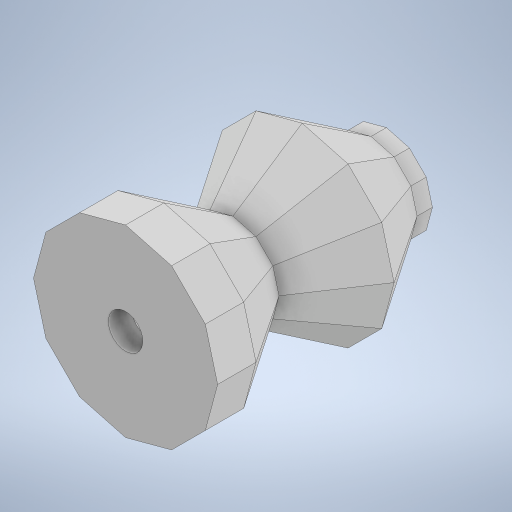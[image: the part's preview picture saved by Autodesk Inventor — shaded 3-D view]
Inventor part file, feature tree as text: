
AUTODESK INVENTOR PART (.ipt)
format: ipt  version: 2023 (Build 270158000, 158)  size: 360,448 bytes
history: native  units: in
note: dims shown in document units (in); Inventor stores cm internally (conversion verified against a paired STEP export)
features: sketch x6, extrude x4, projected_geometry x3, other x2, mirror x2, loft x1, shell x1
ambient origin geometry x8: Origin, YZ Plane, XZ Plane, XY Plane, X Axis, Y Axis, Z Axis, Center Point
bodies: Body1 (feature_tree)
feature tree (19):
  other  "솔리드1"
  sketch  "스케치1"
  other  "작업 평면1"
  loft  "로프트1"
  mirror  "미러1"
  mirror  "미러2"
  extrude  "돌출1"  Depth=0.3543in
  shell  "쉘4"  Thickness=0.4724in
  extrude  "돌출11"  TaperAngle=0.0deg  [1 undecoded]
  extrude  "돌출12"  TaperAngle=0.0deg  [1 undecoded]
  extrude  "돌출13"  Depth=0.122in TaperAngle=0.0deg
  sketch  "스케치2"
  sketch  "스케치3"
  projected_geometry  "투영된 루프1"
  sketch  "스케치13"
  projected_geometry  "투영된 루프8"
  sketch  "스케치14"
  sketch  "스케치15"
  projected_geometry  "투영된 루프9"
note: 2 required parameter values undecoded (feature->parameter linkage not recoverable at this tier; creation-order binding heuristic only, values carry confidence <= 0.55)
